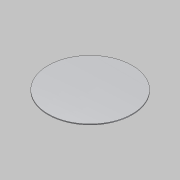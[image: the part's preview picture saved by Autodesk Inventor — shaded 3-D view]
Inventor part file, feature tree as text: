
AUTODESK INVENTOR PART (.ipt)
format: ipt  version: unknown  size: 156,672 bytes
history: native  units: mm
features: extrude x1, sketch x1
ambient origin geometry x8: Origin, YZ Plane, XZ Plane, XY Plane, X Axis, Y Axis, Z Axis, Center Point
feature tree (2):
  extrude  "Выдавливание1"  Depth=5.0mm
  sketch  "Эскиз1"
